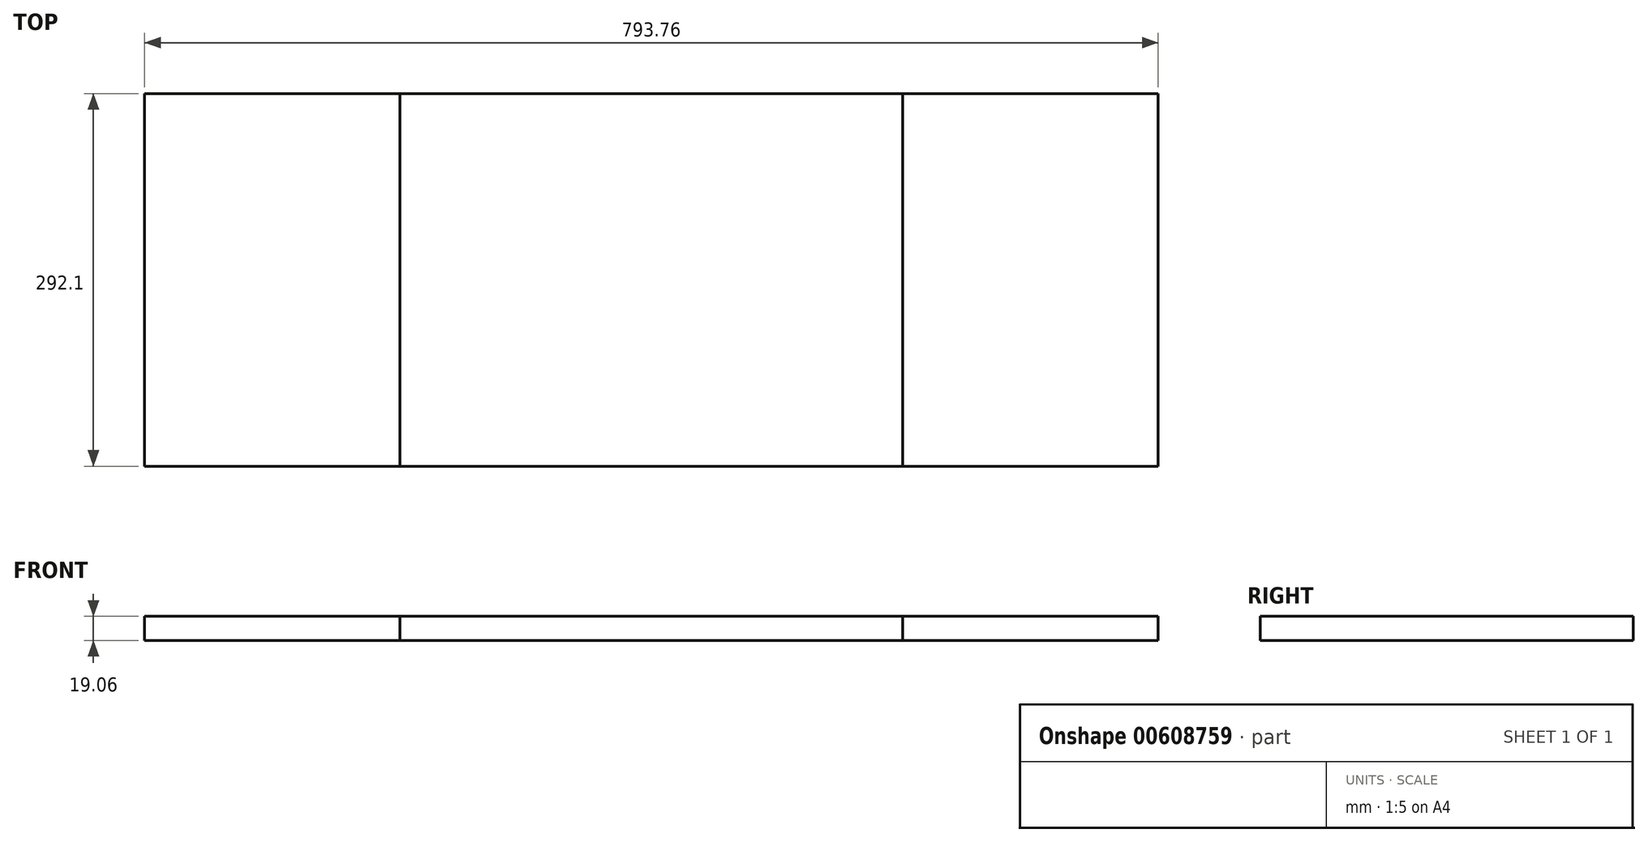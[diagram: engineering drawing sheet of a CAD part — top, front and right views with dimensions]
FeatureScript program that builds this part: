
annotation { "Feature Type Name" : "Feature", "Feature Type Description" : "" }
export const myFeature = defineFeature(function(context is Context, id is Id, definition is map)
    precondition{}
    {
        {
            var Q0;
            Q0=qCreatedBy(makeId("Right.planeOp"),FACE);
            var sketch = newSketch(context, id + "F0", { "sketchPlane" : qUnion([Q0])});
            skLineSegment(sketch, "E0.bottom", {"start": v(146.05, -9.52) * mm, "end": v(-146.05, -9.53) * mm});
            skLineSegment(sketch, "E0.top", {"start": v(146.05, 9.53) * mm, "end": v(-146.05, 9.53) * mm});
            skLineSegment(sketch, "E0.left", {"start": v(146.05, -9.52) * mm, "end": v(146.05, 9.53) * mm});
            skLineSegment(sketch, "E0.right", {"start": v(-146.05, -9.53) * mm, "end": v(-146.05, 9.52) * mm});
            skPoint(sketch, "E0.middle", {"position": v(0, 0) * mm});
            skSolve(sketch);
        }
        {
            var Q0;
            Q0=makeQuery(id+"F0.imprint","IMPRINT",FACE,{"disambiguationData":[TD([[makeQuery(id+"F0.imprint","IMPRINT",EDGE,{"derivedFrom":sQuery(id+"F0.wireOp",EDGE,"E0.bottom")}),-1.0]])]});
            extrude(context, id + "F1", {"entities" : qUnion([Q0]), "endBound" : BoundingType.SYMMETRIC, "depth" : 393.7 * mm, "offsetDistance" : 25.4 * mm});
        }
        {
            var Q0;
            Q0=makeQuery(id+"F0.imprint","IMPRINT",FACE,{"disambiguationData":[TD([[makeQuery(id+"F0.imprint","IMPRINT",EDGE,{"derivedFrom":sQuery(id+"F0.wireOp",EDGE,"E0.bottom")}),-1.0]])]});
            extrude(context, id + "F2", {"entities" : qUnion([Q0]), "endBound" : BoundingType.SYMMETRIC, "depth" : 793.75 * mm, "offsetDistance" : 25.4 * mm});
        }
    });
